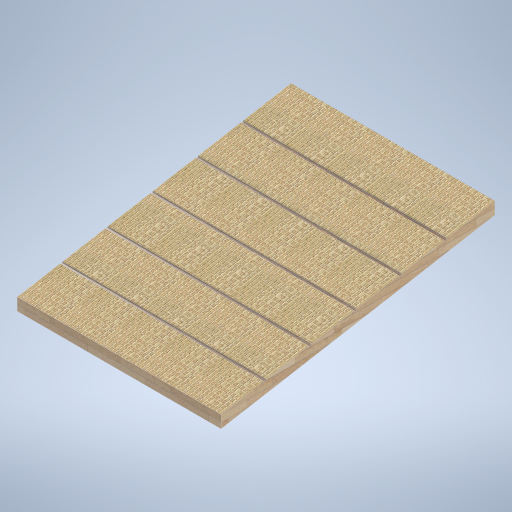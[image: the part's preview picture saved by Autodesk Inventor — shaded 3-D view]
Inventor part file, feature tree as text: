
AUTODESK INVENTOR PART (.ipt)
format: ipt  version: 2024.2 (Build 282272000, 272)  size: 502,272 bytes
history: native  units: mm
features: sketch x5, plane x3, loft x1, extrude x1, projected_geometry x1
ambient origin geometry x8: Origin, YZ Plane, XZ Plane, XY Plane, X Axis, Y Axis, Z Axis, Center Point
bodies: Solid1 (feature_tree)
feature tree (11):
  sketch  "Sketch1"  dims[d0=1644.0mm d1=100.0mm]
  plane  "Work Plane2"
  sketch  "Sketch2"  dims[d2=0.0mm d3=2209.0mm d4=17.453293mm]
  plane  "Work Plane3"
  sketch  "Sketch3"  dims[d5=17.453293mm]
  loft  "Loft1"
  extrude  "Extrusion1"  Depth=2209.0mm
  plane  "Work Plane1"
  sketch  "Sketch4"  dims[d6=1644.0mm]
  sketch  "Sketch5"  dims[d7=0.0mm d8=90.0deg d9=0.0mm d10=90.0deg d11=350.0mm d12=350.0mm d13=350.0mm d14=350.0mm d15=350.0mm d16=0.0mm d17=0.0mm]
  projected_geometry  "Projected Loop1"
